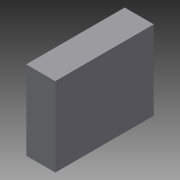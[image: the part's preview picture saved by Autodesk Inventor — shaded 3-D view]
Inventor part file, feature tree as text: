
AUTODESK INVENTOR PART (.ipt)
format: ipt  version: 2015 (Build 190159000, 159)  size: 68,608 bytes
history: native  units: mm
features: extrude x1, sketch x1
ambient origin geometry x8: Origin, YZ Plane, XZ Plane, XY Plane, X Axis, Y Axis, Z Axis, Center Point
bodies: Solid1 (feature_tree)
feature tree (2):
  extrude  "Extrusion1"  Depth=101.5mm
  sketch  "Sketch1"  dims[d0=81.5mm d1=101.5mm d2=30.0mm d3=0.0mm]
